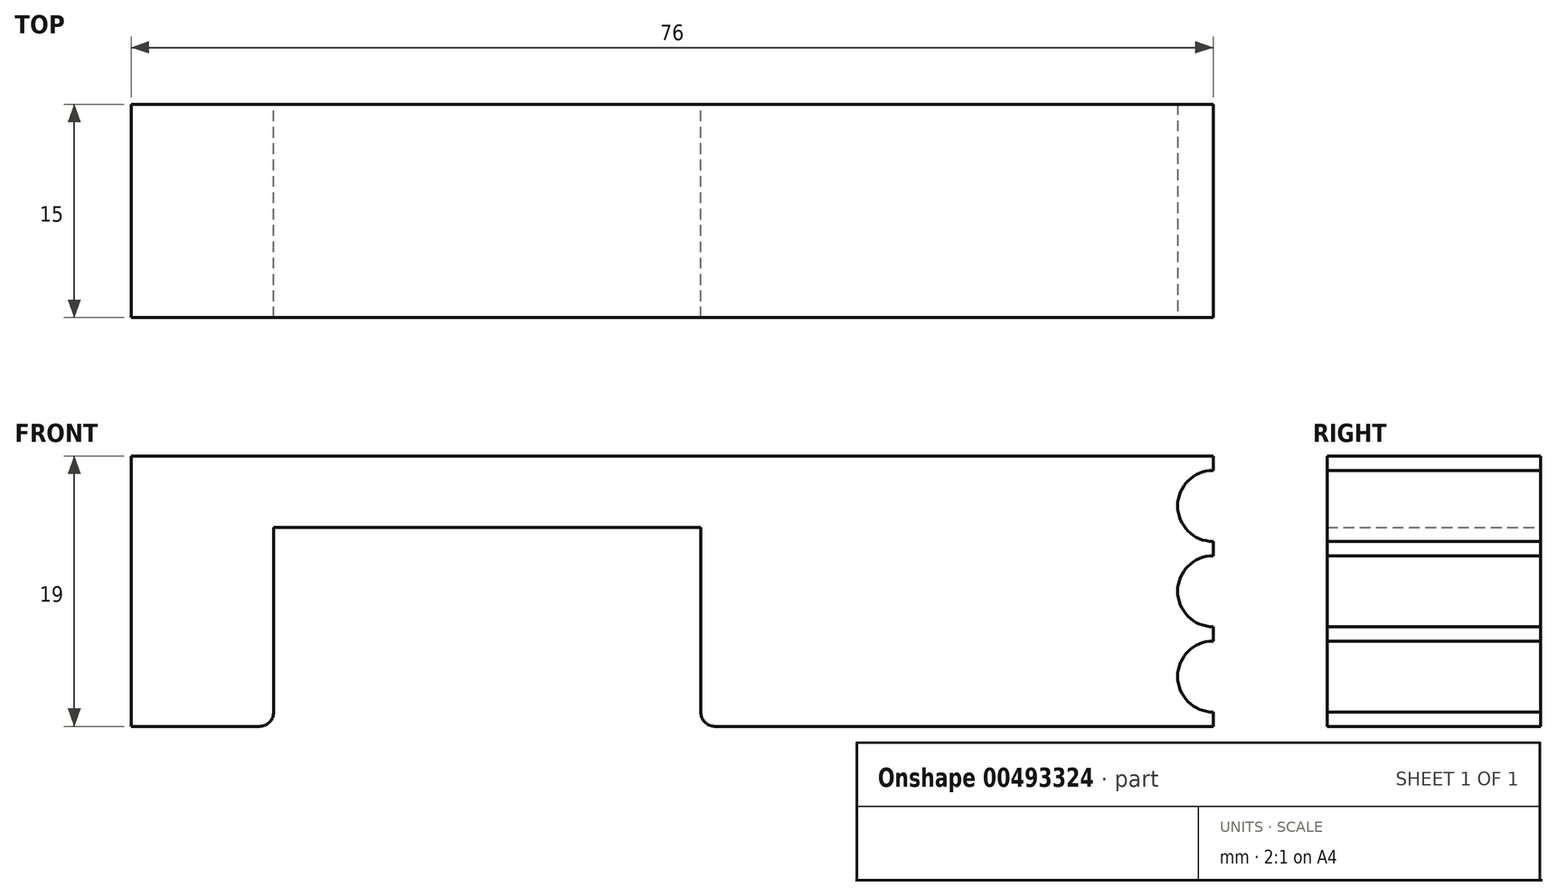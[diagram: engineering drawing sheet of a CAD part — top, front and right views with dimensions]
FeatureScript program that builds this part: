
annotation { "Feature Type Name" : "Feature", "Feature Type Description" : "" }
export const myFeature = defineFeature(function(context is Context, id is Id, definition is map)
    precondition{}
    {
        {
            var Q0;
            Q0=qCreatedBy(makeId("Front.planeOp"),FACE);
            var sketch = newSketch(context, id + "F0", { "sketchPlane" : qUnion([Q0])});
            skLineSegment(sketch, "E0.bottom", {"start": v(-40, 5) * mm, "end": v(36, 5) * mm});
            skLineSegment(sketch, "E0.top", {"start": v(-40, -14) * mm, "end": v(-30, -14) * mm});
            skLineSegment(sketch, "E0.left", {"start": v(-40, 5) * mm, "end": v(-40, -14) * mm});
            skLineSegment(sketch, "E0.right", {"start": v(36, 5) * mm, "end": v(36, -14) * mm});
            skLineSegment(sketch, "E1", {"start": v(-30, -14) * mm, "end": v(-30, 0) * mm});
            skLineSegment(sketch, "E2", {"start": v(-30, 0) * mm, "end": v(0, 0) * mm});
            skLineSegment(sketch, "E3", {"start": v(0, 0) * mm, "end": v(0, -14) * mm});
            skLineSegment(sketch, "E4.trimOffspring", {"start": v(0, -14) * mm, "end": v(36, -14) * mm});
            skSolve(sketch);
        }
        {
            var Q0;
            Q0 = qSketchRegion(id + "F0", true);
            extrude(context, id + "F1", {"entities" : qUnion([Q0]), "depth" : (15 / 2) * mm, "hasSecondDirection" : true, "secondDirectionOppositeDirection" : true, "secondDirectionDepth" : (15 / 2) * mm});
        }
        {
            var Q0;
            Q0=makeQuery(id+"F1.opExtrude","CAP_FACE",FACE,{"disambiguationData":[OSD([sQuery(id+"F0.wireOp",EDGE,"E0.bottom"),sQuery(id+"F0.wireOp",EDGE,"E0.top"),sQuery(id+"F0.wireOp",EDGE,"E0.left"),sQuery(id+"F0.wireOp",EDGE,"E0.right"),sQuery(id+"F0.wireOp",EDGE,"E1"),sQuery(id+"F0.wireOp",EDGE,"E2"),sQuery(id+"F0.wireOp",EDGE,"E3"),sQuery(id+"F0.wireOp",EDGE,"E4.trimOffspring")])],"isStart":false});
            var sketch = newSketch(context, id + "F2", { "sketchPlane" : qUnion([Q0])});
            skCircle(sketch, "E5", {"center": v(36, 1.5) * mm, "radius": 2.5 * mm});
            skCircle(sketch, "E6", {"center": v(36, -4.5) * mm, "radius": 2.5 * mm});
            skCircle(sketch, "E7", {"center": v(36, -10.5) * mm, "radius": 2.5 * mm});
            skSolve(sketch);
        }
        {
            var Q0;
            Q0 = qSketchRegion(id + "F2", true);
            extrude(context, id + "F3", {"entities" : qUnion([Q0]), "operationType" : NewBodyOperationType.REMOVE, "endBound" : BoundingType.THROUGH_ALL, "oppositeDirection" : true, "depth" : 25 * mm});
        }
        {
            var Q0;
            Q0=makeQuery(id+"F1.opExtrude","SWEPT_EDGE",EDGE,{"disambiguationData":[OSD([sQuery(id+"F0.wireOp",EDGE,"E0.top"),sQuery(id+"F0.wireOp",EDGE,"E1")])]});
            var Q1;
            Q1=makeQuery(id+"F1.opExtrude","SWEPT_EDGE",EDGE,{"disambiguationData":[OSD([sQuery(id+"F0.wireOp",EDGE,"E3"),sQuery(id+"F0.wireOp",EDGE,"E4.trimOffspring")])]});
            fillet(context, id + "F4", {"entities" : qUnion([Q0, Q1]), "radius" : 1 * mm, "tangentPropagation" : true, "allowEdgeOverflow" : false});
        }
    });
